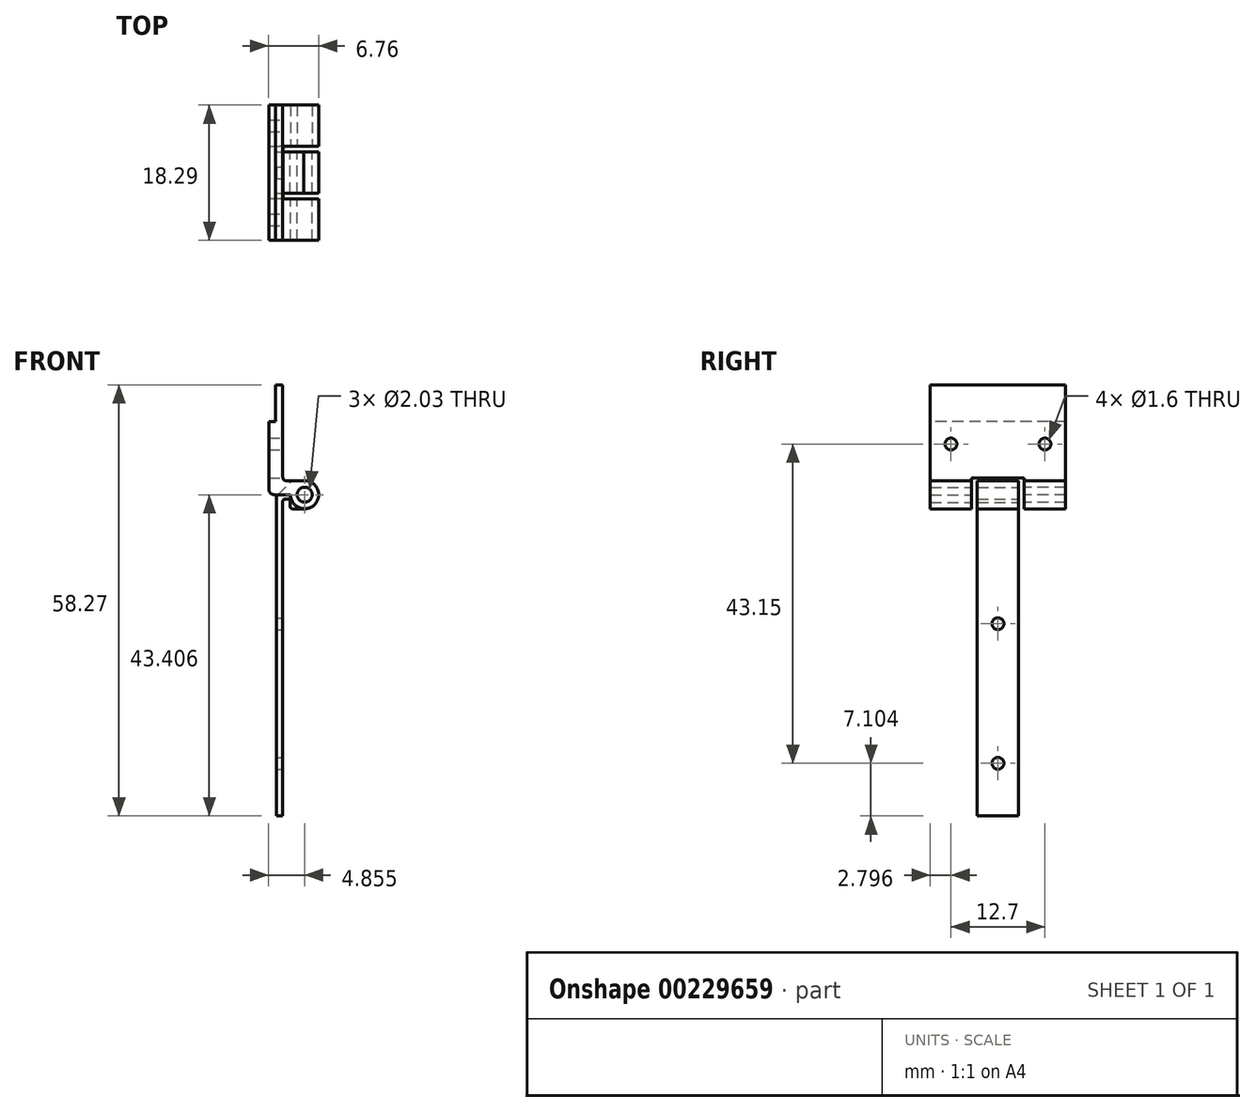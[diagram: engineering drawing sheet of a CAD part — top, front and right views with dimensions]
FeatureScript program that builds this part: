
annotation { "Feature Type Name" : "Feature", "Feature Type Description" : "" }
export const myFeature = defineFeature(function(context is Context, id is Id, definition is map)
    precondition{}
    {
        {
            var Q0;
            Q0=qCreatedBy(makeId("Front.planeOp"),FACE);
            var sketch = newSketch(context, id + "F0", { "sketchPlane" : qUnion([Q0])});
            skLineSegment(sketch, "E0.bottom", {"start": v(0, 0) * mm, "end": v(0.89, 0) * mm});
            skLineSegment(sketch, "E0.left", {"start": v(0, 0) * mm, "end": v(0, 42.9) * mm});
            skLineSegment(sketch, "E0.right", {"start": v(0.89, 0) * mm, "end": v(0.89, 42.54) * mm});
            skLineSegment(sketch, "E1", {"start": v(16.4, 43.4) * mm, "end": v(15.89, 43.4) * mm});
            skLineSegment(sketch, "E2", {"start": v(15.89, 43.4) * mm, "end": v(16.4, 43.4) * mm});
            skArc(sketch, "E3", {"start": v(3.74, 41.5) * mm, "mid": v(5.74, 43.43) * mm, "end": v(3.7, 45.3) * mm});
            skLineSegment(sketch, "E4", {"start": v(1.9, 42.54) * mm, "end": v(1.9, 41.76) * mm});
            skLineSegment(sketch, "E5", {"start": v(3.74, 41.5) * mm, "end": v(2.16, 41.5) * mm});
            skLineSegment(sketch, "E6", {"start": v(1.65, 42.8) * mm, "end": v(1.14, 42.8) * mm});
            skPoint(sketch, "E7.orphan", {"position": v(0.89, 45.31) * mm});
            skLineSegment(sketch, "E8", {"start": v(2.4, 45.3) * mm, "end": v(3.7, 45.3) * mm});
            skLineSegment(sketch, "E9", {"start": v(0.19, 43.35) * mm, "end": v(1.96, 45.12) * mm});
            skPoint(sketch, "E10.visualSharp", {"position": v(2.14, 45.3) * mm});
            skArc(sketch, "E10.filletArc", {"start": v(2.4, 45.3) * mm, "mid": v(2.16, 45.26) * mm, "end": v(1.96, 45.12) * mm});
            skPoint(sketch, "E11.visualSharp", {"position": v(0, 43.16) * mm});
            skArc(sketch, "E11.filletArc", {"start": v(0.19, 43.35) * mm, "mid": v(0.05, 43.14) * mm, "end": v(0, 42.9) * mm});
            skPoint(sketch, "E12.visualSharp", {"position": v(0.89, 42.8) * mm});
            skArc(sketch, "E12.filletArc", {"start": v(1.14, 42.8) * mm, "mid": v(0.96, 42.72) * mm, "end": v(0.89, 42.54) * mm});
            skPoint(sketch, "E13.visualSharp", {"position": v(1.9, 42.8) * mm});
            skArc(sketch, "E13.filletArc", {"start": v(1.9, 42.54) * mm, "mid": v(1.83, 42.72) * mm, "end": v(1.65, 42.8) * mm});
            skPoint(sketch, "E14.visualSharp", {"position": v(1.9, 41.5) * mm});
            skArc(sketch, "E14.filletArc", {"start": v(1.9, 41.76) * mm, "mid": v(1.98, 41.58) * mm, "end": v(2.16, 41.5) * mm});
            skCircle(sketch, "E15", {"center": v(3.84, 43.4) * mm, "radius": 1.02 * mm});
            skSolve(sketch);
        }
        {
            var Q0;
            Q0=makeQuery(id+"F0.imprint","IMPRINT",FACE,{"disambiguationData":[TD([[makeQuery(id+"F0.imprint","IMPRINT",EDGE,{"derivedFrom":sQuery(id+"F0.wireOp",EDGE,"E0.bottom")}),1.0]])]});
            extrude(context, id + "F1", {"entities" : qUnion([Q0]), "depth" : 5.6 * mm});
        }
        {
            var Q0;
            Q0=makeQuery(id+"F1.opExtrude","SWEPT_FACE",FACE,{"disambiguationData":[OSD([sQuery(id+"F0.wireOp",EDGE,"E0.right")])]});
            var sketch = newSketch(context, id + "F2", { "sketchPlane" : qUnion([Q0])});
            skLineSegment(sketch, "E16", {"start": v(-5.59, 25.97) * mm, "end": v(0, 25.97) * mm, "construction": true});
            skLineSegment(sketch, "E17", {"start": v(-5.59, 7.1) * mm, "end": v(0, 7.1) * mm, "construction": true});
            skLineSegment(sketch, "E18", {"start": v(-2.8, 0) * mm, "end": v(-2.8, 29.88) * mm, "construction": true});
            skCircle(sketch, "E19", {"center": v(-2.8, 25.97) * mm, "radius": 0.8 * mm});
            skCircle(sketch, "E20", {"center": v(-2.8, 7.1) * mm, "radius": 0.8 * mm});
            skSolve(sketch);
        }
        {
            var Q0;
            Q0=qSketchRegion(id+"F2",true);
            extrude(context, id + "F3", {"entities" : qUnion([Q0]), "operationType" : NewBodyOperationType.REMOVE, "oppositeDirection" : true, "depth" : 25.4 * mm, "hasSecondDirection" : true, "secondDirectionOppositeDirection" : false, "secondDirectionDepth" : 25.4 * mm});
        }
        {
            var Q0;
            Q0=qCreatedBy(makeId("Front.planeOp"),FACE);
            cPlane(context, id + "F4", {"entities" : qUnion([Q0]), "cplaneType" : CPlaneType.OFFSET, "offset" : 0.76 * mm, "oppositeDirection" : true, "width" : 152.4 * mm, "height" : 152.4 * mm});
        }
        {
            var Q0;
            Q0=qCreatedBy(id+"F4.planeOp",FACE);
            var sketch = newSketch(context, id + "F5", { "sketchPlane" : qUnion([Q0])});
            skCircle(sketch, "E21", {"center": v(3.84, 43.4) * mm, "radius": 1.02 * mm});
            skArc(sketch, "E22", {"start": v(1.93, 43.4) * mm, "mid": v(5.2, 42.07) * mm, "end": v(3.8, 45.31) * mm});
            skLineSegment(sketch, "E23", {"start": v(0.89, 58.27) * mm, "end": v(0.89, 45.27) * mm});
            skLineSegment(sketch, "E24", {"start": v(-1.02, 53.3) * mm, "end": v(-1.02, 43.4) * mm});
            skLineSegment(sketch, "E25", {"start": v(0.89, 58.27) * mm, "end": v(-0.77, 58.27) * mm});
            skLineSegment(sketch, "E26", {"start": v(-0.13, 53.3) * mm, "end": v(-1.02, 53.3) * mm});
            skPoint(sketch, "E27.startSnap0", {"position": v(-0.77, 58.27) * mm});
            skLineSegment(sketch, "E28", {"start": v(-0.13, 58.27) * mm, "end": v(-0.13, 53.3) * mm});
            skPoint(sketch, "E29.orphan", {"position": v(7.54, 58.27) * mm});
            skPoint(sketch, "E30.orphan", {"position": v(-9.08, 58.27) * mm});
            skLineSegment(sketch, "E31", {"start": v(3.8, 45.31) * mm, "end": v(0.89, 45.27) * mm});
            skLineSegment(sketch, "E32", {"start": v(3.84, 43.4) * mm, "end": v(-1.02, 43.4) * mm});
            skSolve(sketch);
        }
        {
            var Q0;
            Q0=makeQuery(id+"F5.imprint","IMPRINT",FACE,{"disambiguationData":[TD([[makeQuery(id+"F5.imprint","IMPRINT",EDGE,{"derivedFrom":sQuery(id+"F5.wireOp",EDGE,"E21")}),-1.0]])]});
            extrude(context, id + "F6", {"entities" : qUnion([Q0]), "oppositeDirection" : true, "depth" : 5.6 * mm});
        }
        {
            var Q0;
            Q0=qCreatedBy(id+"F4.planeOp",FACE);
            cPlane(context, id + "F7", {"entities" : qUnion([Q0]), "cplaneType" : CPlaneType.OFFSET, "offset" : 3.56 * mm, "width" : 152.4 * mm, "height" : 152.4 * mm});
        }
        {
            var Q0;
            Q0=makeQuery(id+"F6.opExtrude","SWEPT_BODY",BODY,{"disambiguationData":[OSD([sQuery(id+"F5.wireOp",EDGE,"E21"),sQuery(id+"F5.wireOp",EDGE,"E22"),sQuery(id+"F5.wireOp",EDGE,"E23"),sQuery(id+"F5.wireOp",EDGE,"E24"),sQuery(id+"F5.wireOp",EDGE,"E25"),sQuery(id+"F5.wireOp",EDGE,"E26"),sQuery(id+"F5.wireOp",EDGE,"E28"),sQuery(id+"F5.wireOp",EDGE,"E31"),sQuery(id+"F5.wireOp",EDGE,"E32")])]});
            var Q1;
            Q1=qCreatedBy(id+"F7.planeOp",FACE);
            mirror(context, id + "F8", {"entities" : qUnion([Q0]), "mirrorPlane" : qUnion([Q1])});
        }
        {
            var Q0;
            Q0=makeQuery(id+"F6.opExtrude","CAP_FACE",FACE,{"disambiguationData":[OSD([sQuery(id+"F5.wireOp",EDGE,"E21"),sQuery(id+"F5.wireOp",EDGE,"E22"),sQuery(id+"F5.wireOp",EDGE,"E23"),sQuery(id+"F5.wireOp",EDGE,"E24"),sQuery(id+"F5.wireOp",EDGE,"E25"),sQuery(id+"F5.wireOp",EDGE,"E26"),sQuery(id+"F5.wireOp",EDGE,"E28"),sQuery(id+"F5.wireOp",EDGE,"E31"),sQuery(id+"F5.wireOp",EDGE,"E32")])],"isStart":true});
            var sketch = newSketch(context, id + "F9", { "sketchPlane" : qUnion([Q0])});
            skLineSegment(sketch, "E33", {"start": v(-1.02, 45.66) * mm, "end": v(0.89, 45.66) * mm});
            skSolve(sketch);
        }
        {
            var Q0;
            {var subQ2=sQuery(id+"F9.wireOp",EDGE,"E33");Q0=makeQuery(id+"F9.imprint","IMPRINT",FACE,{"disambiguationData":[TD([[makeQuery(id+"F9.imprint","IMPRINT",EDGE,{"derivedFrom":subQ2}),1.0]])]});}
            extrude(context, id + "F10", {"entities" : qUnion([Q0]), "endBound" : BoundingType.UP_TO_NEXT, "depth" : 25.4 * mm});
        }
        {
            var Q0;
            Q0=makeQuery(id+"F6.opExtrude","SWEPT_BODY",BODY,{"disambiguationData":[OSD([sQuery(id+"F5.wireOp",EDGE,"E21"),sQuery(id+"F5.wireOp",EDGE,"E22"),sQuery(id+"F5.wireOp",EDGE,"E23"),sQuery(id+"F5.wireOp",EDGE,"E24"),sQuery(id+"F5.wireOp",EDGE,"E25"),sQuery(id+"F5.wireOp",EDGE,"E26"),sQuery(id+"F5.wireOp",EDGE,"E28"),sQuery(id+"F5.wireOp",EDGE,"E31"),sQuery(id+"F5.wireOp",EDGE,"E32")])]});
            var Q1;
            Q1=makeQuery(id+"F10.opExtrude","SWEPT_BODY",BODY,{"disambiguationData":[OSD([sQuery(id+"F5.wireOp",EDGE,"E23"),sQuery(id+"F5.wireOp",EDGE,"E24"),sQuery(id+"F5.wireOp",EDGE,"E25"),sQuery(id+"F5.wireOp",EDGE,"E26"),sQuery(id+"F5.wireOp",EDGE,"E28"),sQuery(id+"F9.wireOp",EDGE,"E33")])]});
            var Q2;
            Q2=makeQuery(id+"F8.opPattern","COPY",BODY,{"derivedFrom":makeQuery(id+"F6.opExtrude","SWEPT_BODY",BODY,{"disambiguationData":[OSD([sQuery(id+"F5.wireOp",EDGE,"E21"),sQuery(id+"F5.wireOp",EDGE,"E22"),sQuery(id+"F5.wireOp",EDGE,"E23"),sQuery(id+"F5.wireOp",EDGE,"E24"),sQuery(id+"F5.wireOp",EDGE,"E25"),sQuery(id+"F5.wireOp",EDGE,"E26"),sQuery(id+"F5.wireOp",EDGE,"E28"),sQuery(id+"F5.wireOp",EDGE,"E31"),sQuery(id+"F5.wireOp",EDGE,"E32")])]}),"instanceName":"1"});
            booleanBodies(context, id + "F11", {"operationType" : BooleanOperationType.UNION, "tools" : qUnion([Q0, Q1, Q2])});
        }
        {
            var Q0;
            Q0=makeQuery(id+"F6.opExtrude","SWEPT_EDGE",EDGE,{"disambiguationData":[OSD([sQuery(id+"F5.wireOp",EDGE,"E23"),sQuery(id+"F5.wireOp",EDGE,"E31")])]});
            fillet(context, id + "F12", {"entities" : qUnion([Q0]), "radius" : 0.5 * mm, "tangentPropagation" : true, "allowEdgeOverflow" : false});
        }
        {
            var Q0;
            Q0=makeQuery(id+"F8.opPattern","COPY",EDGE,{"derivedFrom":makeQuery(id+"F6.opExtrude","SWEPT_EDGE",EDGE,{"disambiguationData":[OSD([sQuery(id+"F5.wireOp",EDGE,"E24"),sQuery(id+"F5.wireOp",EDGE,"E32")])]}),"instanceName":"1"});
            var Q1;
            Q1=makeQuery(id+"F6.opExtrude","SWEPT_EDGE",EDGE,{"disambiguationData":[OSD([sQuery(id+"F5.wireOp",EDGE,"E24"),sQuery(id+"F5.wireOp",EDGE,"E32")])]});
            fillet(context, id + "F13", {"entities" : qUnion([Q0, Q1]), "radius" : 0.76 * mm, "tangentPropagation" : true, "allowEdgeOverflow" : false});
        }
        {
            var Q0;
            {var subQ0=sQuery(id+"F5.wireOp",EDGE,"E23");var subQ1=makeQuery(id+"F6.opExtrude","SWEPT_FACE",FACE,{"disambiguationData":[OSD([subQ0])]});Q0=makeQuery(id+"F11.opBoolean","MERGE",FACE,{"derivedFrom":[subQ1,makeQuery(id+"F8.opPattern","COPY",FACE,{"derivedFrom":subQ1,"instanceName":"1"}),makeQuery(id+"F10.opExtrude","SWEPT_FACE",FACE,{"disambiguationData":[OSD([subQ0])]})]});}
            var sketch = newSketch(context, id + "F14", { "sketchPlane" : qUnion([Q0])});
            skCircle(sketch, "E34", {"center": v(-9.14, 50.25) * mm, "radius": 0.8 * mm});
            skCircle(sketch, "E35", {"center": v(3.56, 50.25) * mm, "radius": 0.8 * mm});
            skSolve(sketch);
        }
        {
            var Q0;
            Q0=makeQuery(id+"F14.imprint","IMPRINT",FACE,{"disambiguationData":[TD([[makeQuery(id+"F14.imprint","IMPRINT",EDGE,{"derivedFrom":sQuery(id+"F14.wireOp",EDGE,"E34")}),1.0]])]});
            extrude(context, id + "F15", {"entities" : qUnion([Q0]), "operationType" : NewBodyOperationType.REMOVE, "oppositeDirection" : true, "depth" : 25.4 * mm, "hasSecondDirection" : true, "secondDirectionOppositeDirection" : false, "secondDirectionDepth" : 25.4 * mm});
        }
        {
            var Q0;
            Q0=qSketchRegion(id+"F14",true);
            extrude(context, id + "F16", {"entities" : qUnion([Q0]), "operationType" : NewBodyOperationType.REMOVE, "oppositeDirection" : true, "depth" : 25.4 * mm, "hasSecondDirection" : true, "secondDirectionOppositeDirection" : false, "secondDirectionDepth" : 25.4 * mm});
        }
    });
